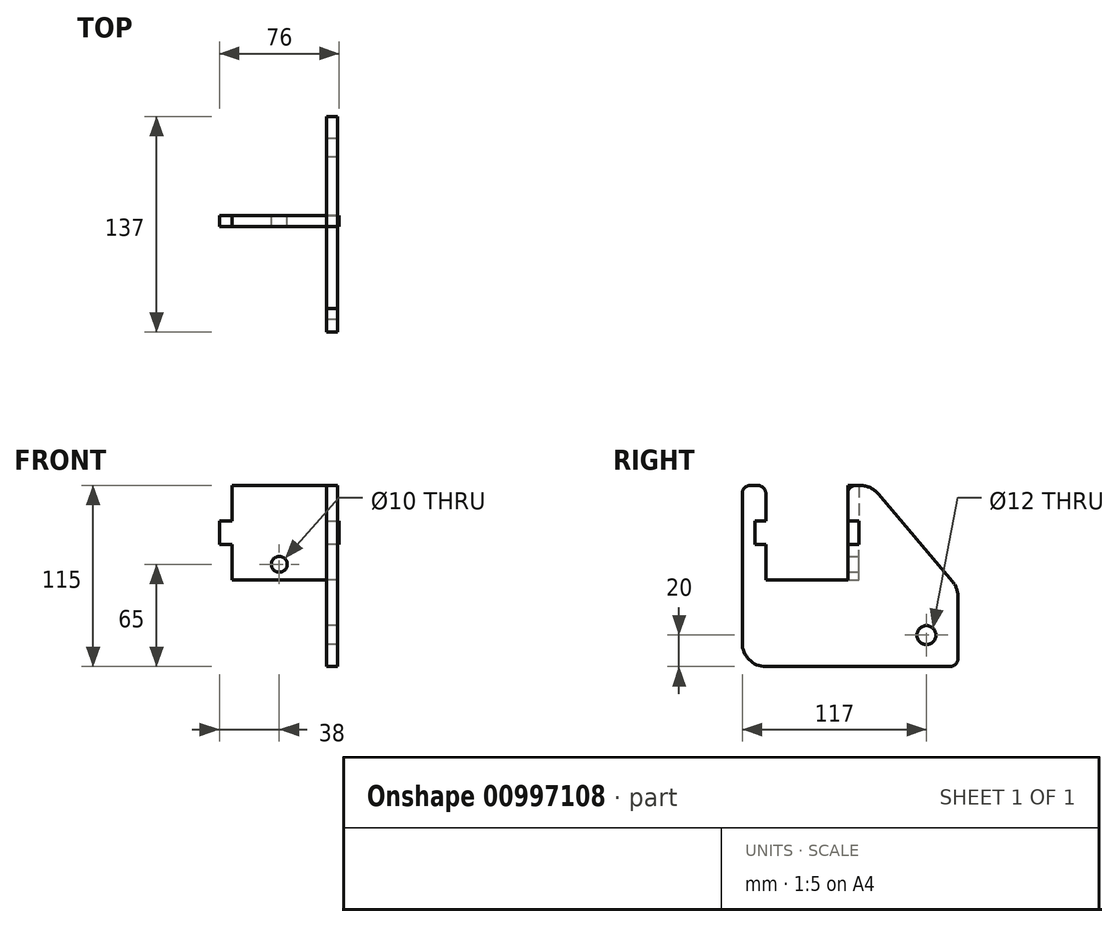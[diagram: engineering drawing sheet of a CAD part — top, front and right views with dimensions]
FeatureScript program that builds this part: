
annotation { "Feature Type Name" : "Feature", "Feature Type Description" : "" }
export const myFeature = defineFeature(function(context is Context, id is Id, definition is map)
    precondition{}
    {
        {
            var Q0;
            Q0=qCreatedBy(makeId("Right.planeOp"),FACE);
            var sketch = newSketch(context, id + "F0", { "sketchPlane" : qUnion([Q0])});
            skCircle(sketch, "E0", {"center": v(0, 0) * mm, "radius": 6 * mm});
            skLineSegment(sketch, "E1", {"start": v(15, -20) * mm, "end": v(-102, -20) * mm});
            skLineSegment(sketch, "E2", {"start": v(-117, -5) * mm, "end": v(-117, 90) * mm});
            skLineSegment(sketch, "E3", {"start": v(-112, 95) * mm, "end": v(-107, 95) * mm});
            skLineSegment(sketch, "E4", {"start": v(-102, 90) * mm, "end": v(-102, 72.5) * mm});
            skLineSegment(sketch, "E5", {"start": v(-102, 35) * mm, "end": v(-50, 35) * mm});
            skLineSegment(sketch, "E6", {"start": v(-50, 35) * mm, "end": v(-50, 57.5) * mm});
            skLineSegment(sketch, "E7", {"start": v(20, 24.5) * mm, "end": v(20, -15) * mm});
            skLineSegment(sketch, "E8", {"start": v(-45, 95) * mm, "end": v(-41.96, 95) * mm});
            skLineSegment(sketch, "E9", {"start": v(-30.5, 89.69) * mm, "end": v(16.45, 34.2) * mm});
            skPoint(sketch, "E10.visualSharp", {"position": v(-117, 95) * mm});
            skArc(sketch, "E10.filletArc", {"start": v(-112, 95) * mm, "mid": v(-115.54, 93.54) * mm, "end": v(-117, 90) * mm});
            skPoint(sketch, "E11.visualSharp", {"position": v(-102, 95) * mm});
            skArc(sketch, "E11.filletArc", {"start": v(-102, 90) * mm, "mid": v(-103.46, 93.54) * mm, "end": v(-107, 95) * mm});
            skPoint(sketch, "E12.visualSharp", {"position": v(-50, 95) * mm});
            skArc(sketch, "E12.filletArc", {"start": v(-45, 95) * mm, "mid": v(-48.54, 93.54) * mm, "end": v(-50, 90) * mm});
            skLineSegment(sketch, "E13", {"start": v(-102, 72.5) * mm, "end": v(-109, 72.5) * mm});
            skLineSegment(sketch, "E14", {"start": v(-109, 72.5) * mm, "end": v(-109, 57.5) * mm});
            skLineSegment(sketch, "E15", {"start": v(-109, 57.5) * mm, "end": v(-102, 57.5) * mm});
            skLineSegment(sketch, "E16", {"start": v(-50, 72.5) * mm, "end": v(-43, 72.5) * mm});
            skLineSegment(sketch, "E17", {"start": v(-43, 72.5) * mm, "end": v(-43, 57.5) * mm});
            skLineSegment(sketch, "E18", {"start": v(-43, 57.5) * mm, "end": v(-50, 57.5) * mm});
            skPoint(sketch, "E19", {"position": v(-109, 65) * mm});
            skLineSegment(sketch, "E20.trimOffspring", {"start": v(-102, 57.5) * mm, "end": v(-102, 35) * mm});
            skLineSegment(sketch, "E21.trimOffspring", {"start": v(-50, 72.5) * mm, "end": v(-50, 90) * mm});
            skPoint(sketch, "E22.visualSharp", {"position": v(-117, -20) * mm});
            skArc(sketch, "E22.filletArc", {"start": v(-117, -5) * mm, "mid": v(-112.6, -15.6) * mm, "end": v(-102, -20) * mm});
            skPoint(sketch, "E23.visualSharp", {"position": v(20, 30) * mm});
            skArc(sketch, "E23.filletArc", {"start": v(20, 24.5) * mm, "mid": v(19.08, 29.66) * mm, "end": v(16.45, 34.2) * mm});
            skPoint(sketch, "E24.visualSharp", {"position": v(20, -20) * mm});
            skArc(sketch, "E24.filletArc", {"start": v(15, -20) * mm, "mid": v(18.54, -18.54) * mm, "end": v(20, -15) * mm});
            skPoint(sketch, "E25.visualSharp", {"position": v(-35, 95) * mm});
            skArc(sketch, "E25.filletArc", {"start": v(-30.5, 89.69) * mm, "mid": v(-35.65, 93.6) * mm, "end": v(-41.96, 95) * mm});
            skSolve(sketch);
        }
        {
            var Q0;
            Q0 = qSketchRegion(id + "F0", true);
            extrude(context, id + "F1", {"entities" : qUnion([Q0]), "depth" : 7 * mm, "offsetDistance" : 25 * mm});
        }
        {
            var Q0;
            Q0=makeQuery(id+"F1.opExtrude","SWEPT_FACE",FACE,{"disambiguationData":[OSD([sQuery(id+"F0.wireOp",EDGE,"E17")])]});
            var sketch = newSketch(context, id + "F2", { "sketchPlane" : qUnion([Q0])});
            skLineSegment(sketch, "E26", {"start": v(8, 72.5) * mm, "end": v(8, 57.5) * mm});
            skLineSegment(sketch, "E27", {"start": v(8, 57.5) * mm, "end": v(0, 57.5) * mm});
            skLineSegment(sketch, "E28", {"start": v(0, 57.5) * mm, "end": v(0, 35) * mm});
            skLineSegment(sketch, "E29", {"start": v(0, 35) * mm, "end": v(-60, 35) * mm});
            skLineSegment(sketch, "E30", {"start": v(-60, 35) * mm, "end": v(-60, 57.5) * mm});
            skLineSegment(sketch, "E31", {"start": v(-60, 57.5) * mm, "end": v(-68, 57.5) * mm});
            skLineSegment(sketch, "E32", {"start": v(-68, 57.5) * mm, "end": v(-68, 72.5) * mm});
            skLineSegment(sketch, "E33", {"start": v(-68, 72.5) * mm, "end": v(-60, 72.5) * mm});
            skLineSegment(sketch, "E34", {"start": v(-60, 72.5) * mm, "end": v(-60, 95) * mm});
            skLineSegment(sketch, "E35", {"start": v(-60, 95) * mm, "end": v(0, 95) * mm});
            skLineSegment(sketch, "E36", {"start": v(0, 95) * mm, "end": v(0, 72.5) * mm});
            skLineSegment(sketch, "E37", {"start": v(0, 72.5) * mm, "end": v(8, 72.5) * mm});
            skPoint(sketch, "E38", {"position": v(-68, 65) * mm});
            skCircle(sketch, "E39", {"center": v(-30, 45) * mm, "radius": 5 * mm});
            skPoint(sketch, "E39.centerSnap0", {"position": v(-30, 35) * mm});
            skSolve(sketch);
        }
        {
            var Q0;
            Q0 = qSketchRegion(id + "F2", true);
            extrude(context, id + "F3", {"entities" : qUnion([Q0]), "depth" : 7 * mm, "offsetDistance" : 25 * mm});
        }
    });
